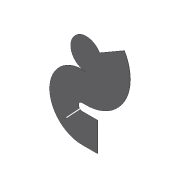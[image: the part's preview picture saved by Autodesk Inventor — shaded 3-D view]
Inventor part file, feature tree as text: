
AUTODESK INVENTOR PART (.ipt)
format: ipt  version: 2012 (Build 160160000, 160)  size: 107,520 bytes
history: native  units: in
note: dims shown in document units (in); Inventor stores cm internally (conversion verified against a paired STEP export)
features: extrude x1, sketch x1
ambient origin geometry x8: Origin, YZ Plane, XZ Plane, XY Plane, X Axis, Y Axis, Z Axis, Center Point
feature tree (2):
  extrude  "Extrusion2"  TaperAngle=60.0deg  [1 undecoded]
  sketch  "Sketch1"  dims[d0=8.0in d2=60.0deg d3=120.0deg d5=27.0in d6=59.0in d7=8.0in d8=22.0in d9=7.5in d14=1.0in d15=37.0in d16=0.1in d17=0.0in d21=1.0in d22=4.0in d25=0.25in]
note: 1 required parameter value undecoded (feature->parameter linkage not recoverable at this tier; creation-order binding heuristic only, values carry confidence <= 0.55)
